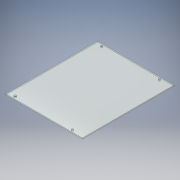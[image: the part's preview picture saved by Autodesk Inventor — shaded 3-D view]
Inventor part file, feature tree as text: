
AUTODESK INVENTOR PART (.ipt)
format: ipt  version: 2019 (Build 230136000, 136)  size: 118,272 bytes
history: native  units: mm
features: extrude x2, sketch x2
ambient origin geometry x8: Origin, YZ Plane, XZ Plane, XY Plane, X Axis, Y Axis, Z Axis, Center Point
bodies: Solid1 (feature_tree)
feature tree (4):
  extrude  "Extrusion1"  Depth=311.0mm
  extrude  "Extrusion2"  TaperAngle=0.0deg  [1 undecoded]
  sketch  "Sketch1"  dims[d0=373.0mm d1=311.0mm]
  sketch  "Sketch2"  dims[d2=300.0mm d3=0.0mm d4=4.0mm d5=0.0mm d6=8.0mm d7=8.0mm d8=9.5mm d9=8.0mm d10=9.5mm d13=12.0mm d14=9.5mm d15=50.0mm d16=50.0mm d17=9.5mm d18=4.0mm d19=0.0mm d20=235.0mm d21=235.0mm]
note: 1 required parameter value undecoded (feature->parameter linkage not recoverable at this tier; creation-order binding heuristic only, values carry confidence <= 0.55)
